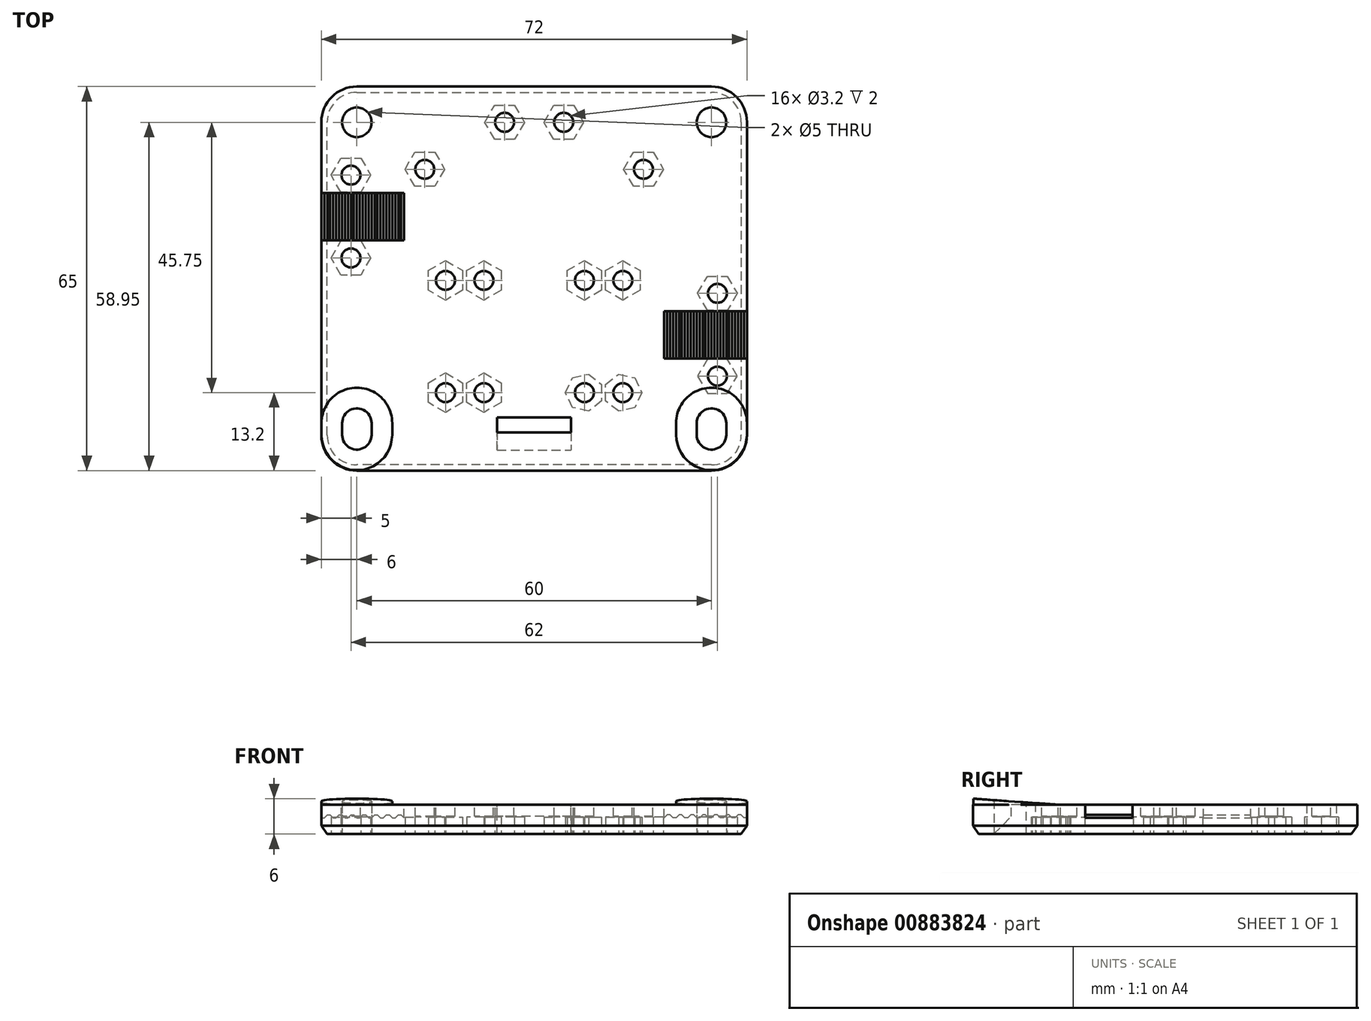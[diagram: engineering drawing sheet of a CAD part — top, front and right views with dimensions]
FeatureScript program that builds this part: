
annotation { "Feature Type Name" : "Feature", "Feature Type Description" : "" }
export const myFeature = defineFeature(function(context is Context, id is Id, definition is map)
    precondition{}
    {
        {
            var Q0;
            Q0=qCreatedBy(makeId("Top.planeOp"),FACE);
            var sketch = newSketch(context, id + "F0", { "sketchPlane" : qUnion([Q0])});
            skPoint(sketch, "E0.0", {"position": v(-36, 32.5) * mm});
            skPoint(sketch, "E0.3", {"position": v(36, 32.5) * mm});
            skPoint(sketch, "E1.1", {"position": v(-36, -32.5) * mm});
            skPoint(sketch, "E1.2", {"position": v(-36, -32.5) * mm});
            skPoint(sketch, "E1.3", {"position": v(36, -32.5) * mm});
            skLineSegment(sketch, "E2", {"start": v(36, -32.5) * mm, "end": v(-36, -32.5) * mm});
            skLineSegment(sketch, "E3", {"start": v(-36, 32.5) * mm, "end": v(36, 32.5) * mm});
            skLineSegment(sketch, "E4", {"start": v(36, 32.5) * mm, "end": v(36, -32.5) * mm});
            skLineSegment(sketch, "E5", {"start": v(-36, 32.5) * mm, "end": v(-36, -32.5) * mm});
            skLineSegment(sketch, "E6", {"start": v(-41.73, 0) * mm, "end": v(49.5, 0) * mm, "construction": true});
            skLineSegment(sketch, "E7", {"start": v(0, 42.12) * mm, "end": v(0, -49.86) * mm, "construction": true});
            skCircle(sketch, "E8", {"center": v(-30, 26.45) * mm, "radius": 2.5 * mm});
            skLineSegment(sketch, "E9", {"start": v(-37.66, 26.45) * mm, "end": v(41.82, 26.45) * mm, "construction": true});
            skLineSegment(sketch, "E10", {"start": v(-30, 35.76) * mm, "end": v(-30, -37.8) * mm, "construction": true});
            skLineSegment(sketch, "E11", {"start": v(30, 35.76) * mm, "end": v(30, -35.32) * mm, "construction": true});
            skPoint(sketch, "E12.0", {"position": v(-32.5, -26.45) * mm});
            skPoint(sketch, "E12.1", {"position": v(-27.5, -26.45) * mm});
            skPoint(sketch, "E13.0", {"position": v(-27.5, -24.45) * mm});
            skPoint(sketch, "E13.1", {"position": v(-32.5, -24.45) * mm});
            skLineSegment(sketch, "E14", {"start": v(-32.5, -24.45) * mm, "end": v(-32.5, -26.45) * mm});
            skLineSegment(sketch, "E15", {"start": v(-27.5, -24.45) * mm, "end": v(-27.5, -26.45) * mm});
            skLineSegment(sketch, "E16", {"start": v(-41.04, -25.45) * mm, "end": v(38.37, -25.45) * mm, "construction": true});
            skPoint(sketch, "E16.startSnap0", {"position": v(-32.5, -25.45) * mm});
            skArc(sketch, "E17", {"start": v(-27.5, -24.45) * mm, "mid": v(-30, -21.95) * mm, "end": v(-32.5, -24.45) * mm});
            skArc(sketch, "E18", {"start": v(-32.5, -26.45) * mm, "mid": v(-30, -28.95) * mm, "end": v(-27.5, -26.45) * mm});
            skLineSegment(sketch, "E19", {"start": v(27.5, -24.45) * mm, "end": v(27.5, -26.45) * mm});
            skLineSegment(sketch, "E20", {"start": v(32.5, -24.45) * mm, "end": v(32.5, -26.45) * mm});
            skArc(sketch, "E21", {"start": v(32.5, -24.45) * mm, "mid": v(30, -21.95) * mm, "end": v(27.5, -24.45) * mm});
            skArc(sketch, "E22", {"start": v(27.5, -26.45) * mm, "mid": v(30, -28.95) * mm, "end": v(32.5, -26.45) * mm});
            skCircle(sketch, "E23", {"center": v(30, 26.45) * mm, "radius": 2.5 * mm});
            skSolve(sketch);
        }
        {
            var Q0;
            Q0=makeQuery(id+"F0.imprint","IMPRINT",FACE,{"disambiguationData":[TD([[makeQuery(id+"F0.imprint","IMPRINT",EDGE,{"derivedFrom":sQuery(id+"F0.wireOp",EDGE,"E2")}),-1.0]])]});
            extrude(context, id + "F1", {"entities" : qUnion([Q0]), "depth" : 5 * mm, "offsetDistance" : 25 * mm});
        }
        {
            var Q0;
            Q0=makeQuery(id+"F1.opExtrude","SWEPT_EDGE",EDGE,{"disambiguationData":[OSD([sQuery(id+"F0.wireOp",EDGE,"E3"),sQuery(id+"F0.wireOp",EDGE,"E5")])]});
            var Q1;
            Q1=makeQuery(id+"F1.opExtrude","SWEPT_EDGE",EDGE,{"disambiguationData":[OSD([sQuery(id+"F0.wireOp",EDGE,"E3"),sQuery(id+"F0.wireOp",EDGE,"E4")])]});
            var Q2;
            Q2=makeQuery(id+"F1.opExtrude","SWEPT_EDGE",EDGE,{"disambiguationData":[OSD([sQuery(id+"F0.wireOp",EDGE,"E2"),sQuery(id+"F0.wireOp",EDGE,"E4")])]});
            var Q3;
            Q3=makeQuery(id+"F1.opExtrude","SWEPT_EDGE",EDGE,{"disambiguationData":[OSD([sQuery(id+"F0.wireOp",EDGE,"E2"),sQuery(id+"F0.wireOp",EDGE,"E5")])]});
            fillet(context, id + "F2", {"entities" : qUnion([Q0, Q1, Q2, Q3]), "radius" : 6 * mm, "tangentPropagation" : true, "allowEdgeOverflow" : false});
        }
        {
            var Q0;
            Q0=makeQuery(id+"F1.opExtrude","CAP_FACE",FACE,{"disambiguationData":[OSD([sQuery(id+"F0.wireOp",EDGE,"E2"),sQuery(id+"F0.wireOp",EDGE,"E3"),sQuery(id+"F0.wireOp",EDGE,"E4"),sQuery(id+"F0.wireOp",EDGE,"E5"),sQuery(id+"F0.wireOp",EDGE,"E8"),sQuery(id+"F0.wireOp",EDGE,"E14"),sQuery(id+"F0.wireOp",EDGE,"E15"),sQuery(id+"F0.wireOp",EDGE,"E17"),sQuery(id+"F0.wireOp",EDGE,"E18"),sQuery(id+"F0.wireOp",EDGE,"E19"),sQuery(id+"F0.wireOp",EDGE,"E20"),sQuery(id+"F0.wireOp",EDGE,"E21"),sQuery(id+"F0.wireOp",EDGE,"E22"),sQuery(id+"F0.wireOp",EDGE,"E23")])],"isStart":false});
            var sketch = newSketch(context, id + "F3", { "sketchPlane" : qUnion([Q0])});
            skCircle(sketch, "E24", {"center": v(31, -2.5) * mm, "radius": 1.6 * mm});
            skCircle(sketch, "E25", {"center": v(31, -16.5) * mm, "radius": 1.6 * mm});
            skLineSegment(sketch, "E26", {"start": v(36, -5.5) * mm, "end": v(22, -5.5) * mm});
            skLineSegment(sketch, "E27", {"start": v(22, -5.5) * mm, "end": v(22, -13.5) * mm});
            skLineSegment(sketch, "E28", {"start": v(22, -13.5) * mm, "end": v(36, -13.5) * mm});
            skLineSegment(sketch, "E29", {"start": v(36, -13.5) * mm, "end": v(36, -5.5) * mm});
            skLineSegment(sketch, "E30.0", {"start": v(36, 32.5) * mm, "end": v(36, -32.5) * mm});
            skLineSegment(sketch, "E31.bottom", {"start": v(-36, 14.5) * mm, "end": v(-22, 14.5) * mm});
            skLineSegment(sketch, "E31.top", {"start": v(-36, 6.5) * mm, "end": v(-22, 6.5) * mm});
            skLineSegment(sketch, "E31.left", {"start": v(-36, 14.5) * mm, "end": v(-36, 6.5) * mm});
            skLineSegment(sketch, "E31.right", {"start": v(-22, 14.5) * mm, "end": v(-22, 6.5) * mm});
            skLineSegment(sketch, "E32.0", {"start": v(-36, 32.5) * mm, "end": v(-36, -32.5) * mm});
            skCircle(sketch, "E33", {"center": v(-31, 17.5) * mm, "radius": 1.6 * mm});
            skCircle(sketch, "E34", {"center": v(-31, 3.5) * mm, "radius": 1.6 * mm});
            skCircle(sketch, "E35", {"center": v(-5, 26.45) * mm, "radius": 1.6 * mm});
            skCircle(sketch, "E36", {"center": v(5, 26.45) * mm, "radius": 1.6 * mm});
            skCircle(sketch, "E37", {"center": v(-8.5, -0.3) * mm, "radius": 1.6 * mm});
            skCircle(sketch, "E38", {"center": v(8.5, -0.3) * mm, "radius": 1.6 * mm});
            skCircle(sketch, "E39", {"center": v(-8.5, -19.3) * mm, "radius": 1.6 * mm});
            skCircle(sketch, "E40", {"center": v(8.5, -19.3) * mm, "radius": 1.6 * mm});
            skCircle(sketch, "E41", {"center": v(15, -0.3) * mm, "radius": 1.6 * mm});
            skCircle(sketch, "E42", {"center": v(15, -19.3) * mm, "radius": 1.6 * mm});
            skCircle(sketch, "E43", {"center": v(-15, -19.3) * mm, "radius": 1.6 * mm});
            skCircle(sketch, "E44", {"center": v(-15, -0.3) * mm, "radius": 1.6 * mm});
            skArc(sketch, "E45.0", {"start": v(-24, -24.45) * mm, "mid": v(-30, -18.45) * mm, "end": v(-36, -24.45) * mm});
            skLineSegment(sketch, "E45.1", {"start": v(-24, -24.45) * mm, "end": v(-24, -26.45) * mm});
            skArc(sketch, "E45.2", {"start": v(-36, -26.45) * mm, "mid": v(-30, -32.45) * mm, "end": v(-24, -26.45) * mm});
            skLineSegment(sketch, "E45.3", {"start": v(-36, -24.45) * mm, "end": v(-36, -26.45) * mm});
            skArc(sketch, "E46.0", {"start": v(36, -24.45) * mm, "mid": v(30, -18.45) * mm, "end": v(24, -24.45) * mm});
            skLineSegment(sketch, "E46.1", {"start": v(36, -24.45) * mm, "end": v(36, -26.45) * mm});
            skArc(sketch, "E46.2", {"start": v(24, -26.45) * mm, "mid": v(30, -32.45) * mm, "end": v(36, -26.45) * mm});
            skLineSegment(sketch, "E46.3", {"start": v(24, -24.45) * mm, "end": v(24, -26.45) * mm});
            skCircle(sketch, "E47", {"center": v(13, -26.5) * mm, "radius": 1.6 * mm});
            skCircle(sketch, "E48", {"center": v(-13, -26.5) * mm, "radius": 1.6 * mm});
            skLineSegment(sketch, "E49.bottom", {"start": v(-6.25, -23.5) * mm, "end": v(6.25, -23.5) * mm});
            skLineSegment(sketch, "E49.top", {"start": v(-6.25, -26) * mm, "end": v(6.25, -26) * mm});
            skLineSegment(sketch, "E49.left", {"start": v(-6.25, -23.5) * mm, "end": v(-6.25, -26) * mm});
            skLineSegment(sketch, "E49.right", {"start": v(6.25, -23.5) * mm, "end": v(6.25, -26) * mm});
            skCircle(sketch, "E50", {"center": v(-18.5, 18.5) * mm, "radius": 1.6 * mm});
            skCircle(sketch, "E51", {"center": v(18.5, 18.5) * mm, "radius": 1.6 * mm});
            skSolve(sketch);
        }
        {
            var Q0;
            {var subQ0=sQuery(id+"F3.wireOp",EDGE,"E31.bottom");Q0=makeQuery(id+"F3.imprint","IMPRINT",FACE,{"disambiguationData":[TD([[makeQuery(id+"F3.imprint","IMPRINT",EDGE,{"derivedFrom":subQ0}),-1.0]])]});}
            var Q1;
            {var subQ0=sQuery(id+"F3.wireOp",EDGE,"E26");Q1=makeQuery(id+"F3.imprint","IMPRINT",FACE,{"disambiguationData":[TD([[makeQuery(id+"F3.imprint","IMPRINT",EDGE,{"derivedFrom":subQ0}),1.0]])]});}
            extrude(context, id + "F4", {"entities" : qUnion([Q0, Q1]), "operationType" : NewBodyOperationType.REMOVE, "oppositeDirection" : true, "depth" : 2.25 * mm, "offsetDistance" : 25 * mm});
        }
        {
            var Q0;
            Q0=makeQuery(id+"F3.imprint","IMPRINT",FACE,{"disambiguationData":[TD([[makeQuery(id+"F3.imprint","IMPRINT",EDGE,{"derivedFrom":sQuery(id+"F3.wireOp",EDGE,"E36")}),1.0]])]});
            var Q1;
            Q1=makeQuery(id+"F3.imprint","IMPRINT",FACE,{"disambiguationData":[TD([[makeQuery(id+"F3.imprint","IMPRINT",EDGE,{"derivedFrom":sQuery(id+"F3.wireOp",EDGE,"E35")}),1.0]])]});
            var Q2;
            Q2=makeQuery(id+"F3.imprint","IMPRINT",FACE,{"disambiguationData":[TD([[makeQuery(id+"F3.imprint","IMPRINT",EDGE,{"derivedFrom":sQuery(id+"F3.wireOp",EDGE,"E33")}),1.0]])]});
            var Q3;
            Q3=makeQuery(id+"F3.imprint","IMPRINT",FACE,{"disambiguationData":[TD([[makeQuery(id+"F3.imprint","IMPRINT",EDGE,{"derivedFrom":sQuery(id+"F3.wireOp",EDGE,"E34")}),1.0]])]});
            var Q4;
            Q4=makeQuery(id+"F3.imprint","IMPRINT",FACE,{"disambiguationData":[TD([[makeQuery(id+"F3.imprint","IMPRINT",EDGE,{"derivedFrom":sQuery(id+"F3.wireOp",EDGE,"E24")}),1.0]])]});
            var Q5;
            Q5=makeQuery(id+"F3.imprint","IMPRINT",FACE,{"disambiguationData":[TD([[makeQuery(id+"F3.imprint","IMPRINT",EDGE,{"derivedFrom":sQuery(id+"F3.wireOp",EDGE,"E25")}),1.0]])]});
            var Q6;
            Q6=makeQuery(id+"F3.imprint","IMPRINT",FACE,{"disambiguationData":[TD([[makeQuery(id+"F3.imprint","IMPRINT",EDGE,{"derivedFrom":sQuery(id+"F3.wireOp",EDGE,"E44")}),1.0]])]});
            var Q7;
            Q7=makeQuery(id+"F3.imprint","IMPRINT",FACE,{"disambiguationData":[TD([[makeQuery(id+"F3.imprint","IMPRINT",EDGE,{"derivedFrom":sQuery(id+"F3.wireOp",EDGE,"E37")}),1.0]])]});
            var Q8;
            Q8=makeQuery(id+"F3.imprint","IMPRINT",FACE,{"disambiguationData":[TD([[makeQuery(id+"F3.imprint","IMPRINT",EDGE,{"derivedFrom":sQuery(id+"F3.wireOp",EDGE,"E38")}),1.0]])]});
            var Q9;
            Q9=makeQuery(id+"F3.imprint","IMPRINT",FACE,{"disambiguationData":[TD([[makeQuery(id+"F3.imprint","IMPRINT",EDGE,{"derivedFrom":sQuery(id+"F3.wireOp",EDGE,"E41")}),1.0]])]});
            var Q10;
            Q10=makeQuery(id+"F3.imprint","IMPRINT",FACE,{"disambiguationData":[TD([[makeQuery(id+"F3.imprint","IMPRINT",EDGE,{"derivedFrom":sQuery(id+"F3.wireOp",EDGE,"E42")}),1.0]])]});
            var Q11;
            Q11=makeQuery(id+"F3.imprint","IMPRINT",FACE,{"disambiguationData":[TD([[makeQuery(id+"F3.imprint","IMPRINT",EDGE,{"derivedFrom":sQuery(id+"F3.wireOp",EDGE,"E40")}),1.0]])]});
            var Q12;
            Q12=makeQuery(id+"F3.imprint","IMPRINT",FACE,{"disambiguationData":[TD([[makeQuery(id+"F3.imprint","IMPRINT",EDGE,{"derivedFrom":sQuery(id+"F3.wireOp",EDGE,"E39")}),1.0]])]});
            var Q13;
            Q13=makeQuery(id+"F3.imprint","IMPRINT",FACE,{"disambiguationData":[TD([[makeQuery(id+"F3.imprint","IMPRINT",EDGE,{"derivedFrom":sQuery(id+"F3.wireOp",EDGE,"E43")}),1.0]])]});
            var Q14;
            Q14=makeQuery(id+"F3.imprint","IMPRINT",FACE,{"disambiguationData":[TD([[makeQuery(id+"F3.imprint","IMPRINT",EDGE,{"derivedFrom":sQuery(id+"F3.wireOp",EDGE,"E50")}),1.0]])]});
            var Q15;
            Q15=makeQuery(id+"F3.imprint","IMPRINT",FACE,{"disambiguationData":[TD([[makeQuery(id+"F3.imprint","IMPRINT",EDGE,{"derivedFrom":sQuery(id+"F3.wireOp",EDGE,"E51")}),1.0]])]});
            extrude(context, id + "F5", {"entities" : qUnion([Q0, Q1, Q2, Q3, Q4, Q5, Q6, Q7, Q8, Q9, Q10, Q11, Q12, Q13, Q14, Q15]), "operationType" : NewBodyOperationType.REMOVE, "oppositeDirection" : true, "depth" : 2 * mm, "offsetDistance" : 25 * mm});
        }
        {
            var Q0;
            Q0=makeQuery(id+"F0.imprint","IMPRINT",FACE,{"disambiguationData":[TD([[makeQuery(id+"F0.imprint","IMPRINT",EDGE,{"derivedFrom":sQuery(id+"F0.wireOp",EDGE,"E2")}),-1.0]])]});
            var sketch = newSketch(context, id + "F6", { "sketchPlane" : qUnion([Q0])});
            skCircle(sketch, "E52.cCircle", {"center": v(31, -16.5) * mm, "radius": 2.9 * mm, "construction": true});
            skLineSegment(sketch, "E52.0", {"start": v(32.67, -13.6) * mm, "end": v(29.33, -13.6) * mm});
            skLineSegment(sketch, "E52.1", {"start": v(34.35, -16.5) * mm, "end": v(32.67, -13.6) * mm});
            skLineSegment(sketch, "E52.2", {"start": v(32.67, -19.4) * mm, "end": v(34.35, -16.5) * mm});
            skLineSegment(sketch, "E52.3", {"start": v(29.33, -19.4) * mm, "end": v(32.67, -19.4) * mm});
            skLineSegment(sketch, "E52.4", {"start": v(27.65, -16.5) * mm, "end": v(29.33, -19.4) * mm});
            skLineSegment(sketch, "E52.5", {"start": v(29.33, -13.6) * mm, "end": v(27.65, -16.5) * mm});
            skPoint(sketch, "E52.0.midPoint", {"position": v(31, -13.6) * mm});
            skCircle(sketch, "E53.cCircle", {"center": v(31, -2.5) * mm, "radius": 2.9 * mm, "construction": true});
            skLineSegment(sketch, "E53.0", {"start": v(32.67, -5.4) * mm, "end": v(29.33, -5.4) * mm});
            skLineSegment(sketch, "E53.1", {"start": v(29.33, -5.4) * mm, "end": v(27.65, -2.5) * mm});
            skLineSegment(sketch, "E53.2", {"start": v(27.65, -2.5) * mm, "end": v(29.33, 0.4) * mm});
            skLineSegment(sketch, "E53.3", {"start": v(29.33, 0.4) * mm, "end": v(32.67, 0.4) * mm});
            skLineSegment(sketch, "E53.4", {"start": v(32.67, 0.4) * mm, "end": v(34.35, -2.5) * mm});
            skLineSegment(sketch, "E53.5", {"start": v(34.35, -2.5) * mm, "end": v(32.67, -5.4) * mm});
            skPoint(sketch, "E53.0.midPoint", {"position": v(31, -5.4) * mm});
            skPoint(sketch, "E54.0", {"position": v(-31, 3.5) * mm});
            skPoint(sketch, "E54.1", {"position": v(-31, 17.5) * mm});
            skPoint(sketch, "E54.2", {"position": v(-5, 26.45) * mm});
            skPoint(sketch, "E54.3", {"position": v(5, 26.45) * mm});
            skCircle(sketch, "E55.cCircle", {"center": v(-31, 3.5) * mm, "radius": 2.9 * mm, "construction": true});
            skLineSegment(sketch, "E55.0", {"start": v(-32.67, 6.4) * mm, "end": v(-29.33, 6.4) * mm});
            skLineSegment(sketch, "E55.1", {"start": v(-29.33, 6.4) * mm, "end": v(-27.65, 3.5) * mm});
            skLineSegment(sketch, "E55.2", {"start": v(-27.65, 3.5) * mm, "end": v(-29.33, 0.6) * mm});
            skLineSegment(sketch, "E55.3", {"start": v(-29.33, 0.6) * mm, "end": v(-32.67, 0.6) * mm});
            skLineSegment(sketch, "E55.4", {"start": v(-32.67, 0.6) * mm, "end": v(-34.35, 3.5) * mm});
            skLineSegment(sketch, "E55.5", {"start": v(-34.35, 3.5) * mm, "end": v(-32.67, 6.4) * mm});
            skPoint(sketch, "E55.0.midPoint", {"position": v(-31, 6.4) * mm});
            skCircle(sketch, "E56.cCircle", {"center": v(-31, 17.5) * mm, "radius": 2.9 * mm, "construction": true});
            skLineSegment(sketch, "E56.0", {"start": v(-32.67, 20.4) * mm, "end": v(-29.33, 20.4) * mm});
            skLineSegment(sketch, "E56.1", {"start": v(-29.33, 20.4) * mm, "end": v(-27.65, 17.5) * mm});
            skLineSegment(sketch, "E56.2", {"start": v(-27.65, 17.5) * mm, "end": v(-29.33, 14.6) * mm});
            skLineSegment(sketch, "E56.3", {"start": v(-29.33, 14.6) * mm, "end": v(-32.67, 14.6) * mm});
            skLineSegment(sketch, "E56.4", {"start": v(-32.67, 14.6) * mm, "end": v(-34.35, 17.5) * mm});
            skLineSegment(sketch, "E56.5", {"start": v(-34.35, 17.5) * mm, "end": v(-32.67, 20.4) * mm});
            skPoint(sketch, "E56.0.midPoint", {"position": v(-31, 20.4) * mm});
            skCircle(sketch, "E57.cCircle", {"center": v(5, 26.45) * mm, "radius": 2.9 * mm, "construction": true});
            skLineSegment(sketch, "E57.0", {"start": v(6.67, 23.55) * mm, "end": v(3.33, 23.55) * mm});
            skLineSegment(sketch, "E57.1", {"start": v(3.33, 23.55) * mm, "end": v(1.65, 26.45) * mm});
            skLineSegment(sketch, "E57.2", {"start": v(1.65, 26.45) * mm, "end": v(3.33, 29.35) * mm});
            skLineSegment(sketch, "E57.3", {"start": v(3.33, 29.35) * mm, "end": v(6.67, 29.35) * mm});
            skLineSegment(sketch, "E57.4", {"start": v(6.67, 29.35) * mm, "end": v(8.35, 26.45) * mm});
            skLineSegment(sketch, "E57.5", {"start": v(8.35, 26.45) * mm, "end": v(6.67, 23.55) * mm});
            skPoint(sketch, "E57.0.midPoint", {"position": v(5, 23.55) * mm});
            skCircle(sketch, "E58.cCircle", {"center": v(-5, 26.45) * mm, "radius": 2.9 * mm, "construction": true});
            skLineSegment(sketch, "E58.0", {"start": v(-3.33, 23.55) * mm, "end": v(-6.67, 23.55) * mm});
            skLineSegment(sketch, "E58.1", {"start": v(-6.67, 23.55) * mm, "end": v(-8.35, 26.45) * mm});
            skLineSegment(sketch, "E58.2", {"start": v(-8.35, 26.45) * mm, "end": v(-6.67, 29.35) * mm});
            skLineSegment(sketch, "E58.3", {"start": v(-6.67, 29.35) * mm, "end": v(-3.33, 29.35) * mm});
            skLineSegment(sketch, "E58.4", {"start": v(-3.33, 29.35) * mm, "end": v(-1.65, 26.45) * mm});
            skLineSegment(sketch, "E58.5", {"start": v(-1.65, 26.45) * mm, "end": v(-3.33, 23.55) * mm});
            skPoint(sketch, "E58.0.midPoint", {"position": v(-5, 23.55) * mm});
            skPoint(sketch, "E59.0", {"position": v(15, -0.3) * mm});
            skPoint(sketch, "E59.1", {"position": v(8.5, -0.3) * mm});
            skPoint(sketch, "E59.2", {"position": v(-8.5, -0.3) * mm});
            skPoint(sketch, "E59.3", {"position": v(-15, -0.3) * mm});
            skPoint(sketch, "E59.4", {"position": v(-15, -19.3) * mm});
            skPoint(sketch, "E59.5", {"position": v(-8.5, -19.3) * mm});
            skPoint(sketch, "E59.6", {"position": v(8.5, -19.3) * mm});
            skPoint(sketch, "E59.7", {"position": v(15, -19.3) * mm});
            skCircle(sketch, "E60.cCircle", {"center": v(15, -0.3) * mm, "radius": 2.9 * mm, "construction": true});
            skLineSegment(sketch, "E60.0", {"start": v(12.1, -1.97) * mm, "end": v(12.1, 1.37) * mm});
            skLineSegment(sketch, "E60.1", {"start": v(12.1, 1.37) * mm, "end": v(15, 3.05) * mm});
            skLineSegment(sketch, "E60.2", {"start": v(15, 3.05) * mm, "end": v(17.9, 1.37) * mm});
            skLineSegment(sketch, "E60.3", {"start": v(17.9, 1.37) * mm, "end": v(17.9, -1.97) * mm});
            skLineSegment(sketch, "E60.4", {"start": v(17.9, -1.97) * mm, "end": v(15, -3.65) * mm});
            skLineSegment(sketch, "E60.5", {"start": v(15, -3.65) * mm, "end": v(12.1, -1.97) * mm});
            skPoint(sketch, "E60.0.midPoint", {"position": v(12.1, -0.3) * mm});
            skCircle(sketch, "E61.cCircle", {"center": v(8.5, -0.3) * mm, "radius": 2.9 * mm, "construction": true});
            skLineSegment(sketch, "E61.0", {"start": v(11.4, 1.37) * mm, "end": v(11.4, -1.97) * mm});
            skLineSegment(sketch, "E61.1", {"start": v(11.4, -1.97) * mm, "end": v(8.5, -3.65) * mm});
            skLineSegment(sketch, "E61.2", {"start": v(8.5, -3.65) * mm, "end": v(5.6, -1.97) * mm});
            skLineSegment(sketch, "E61.3", {"start": v(5.6, -1.97) * mm, "end": v(5.6, 1.37) * mm});
            skLineSegment(sketch, "E61.4", {"start": v(5.6, 1.37) * mm, "end": v(8.5, 3.05) * mm});
            skLineSegment(sketch, "E61.5", {"start": v(8.5, 3.05) * mm, "end": v(11.4, 1.37) * mm});
            skPoint(sketch, "E61.0.midPoint", {"position": v(11.4, -0.3) * mm});
            skCircle(sketch, "E62.cCircle", {"center": v(-8.5, -0.3) * mm, "radius": 2.9 * mm, "construction": true});
            skLineSegment(sketch, "E62.0", {"start": v(-11.4, -1.97) * mm, "end": v(-11.4, 1.37) * mm});
            skLineSegment(sketch, "E62.1", {"start": v(-11.4, 1.37) * mm, "end": v(-8.5, 3.05) * mm});
            skLineSegment(sketch, "E62.2", {"start": v(-8.5, 3.05) * mm, "end": v(-5.6, 1.37) * mm});
            skLineSegment(sketch, "E62.3", {"start": v(-5.6, 1.37) * mm, "end": v(-5.6, -1.97) * mm});
            skLineSegment(sketch, "E62.4", {"start": v(-5.6, -1.97) * mm, "end": v(-8.5, -3.65) * mm});
            skLineSegment(sketch, "E62.5", {"start": v(-8.5, -3.65) * mm, "end": v(-11.4, -1.97) * mm});
            skPoint(sketch, "E62.0.midPoint", {"position": v(-11.4, -0.3) * mm});
            skCircle(sketch, "E63.cCircle", {"center": v(-15, -0.3) * mm, "radius": 2.9 * mm, "construction": true});
            skLineSegment(sketch, "E63.0", {"start": v(-12.1, 1.37) * mm, "end": v(-12.1, -1.97) * mm});
            skLineSegment(sketch, "E63.1", {"start": v(-12.1, -1.97) * mm, "end": v(-15, -3.65) * mm});
            skLineSegment(sketch, "E63.2", {"start": v(-15, -3.65) * mm, "end": v(-17.9, -1.97) * mm});
            skLineSegment(sketch, "E63.3", {"start": v(-17.9, -1.97) * mm, "end": v(-17.9, 1.37) * mm});
            skLineSegment(sketch, "E63.4", {"start": v(-17.9, 1.37) * mm, "end": v(-15, 3.05) * mm});
            skLineSegment(sketch, "E63.5", {"start": v(-15, 3.05) * mm, "end": v(-12.1, 1.37) * mm});
            skPoint(sketch, "E63.0.midPoint", {"position": v(-12.1, -0.3) * mm});
            skCircle(sketch, "E64.cCircle", {"center": v(-15, -19.3) * mm, "radius": 2.9 * mm, "construction": true});
            skLineSegment(sketch, "E64.0", {"start": v(-12.1, -17.63) * mm, "end": v(-12.1, -20.97) * mm});
            skLineSegment(sketch, "E64.1", {"start": v(-12.1, -20.97) * mm, "end": v(-15, -22.65) * mm});
            skLineSegment(sketch, "E64.2", {"start": v(-15, -22.65) * mm, "end": v(-17.9, -20.97) * mm});
            skLineSegment(sketch, "E64.3", {"start": v(-17.9, -20.97) * mm, "end": v(-17.9, -17.63) * mm});
            skLineSegment(sketch, "E64.4", {"start": v(-17.9, -17.63) * mm, "end": v(-15, -15.95) * mm});
            skLineSegment(sketch, "E64.5", {"start": v(-15, -15.95) * mm, "end": v(-12.1, -17.63) * mm});
            skPoint(sketch, "E64.0.midPoint", {"position": v(-12.1, -19.3) * mm});
            skCircle(sketch, "E65.cCircle", {"center": v(-8.5, -19.3) * mm, "radius": 2.9 * mm, "construction": true});
            skLineSegment(sketch, "E65.0", {"start": v(-11.4, -20.97) * mm, "end": v(-11.4, -17.63) * mm});
            skLineSegment(sketch, "E65.1", {"start": v(-11.4, -17.63) * mm, "end": v(-8.5, -15.95) * mm});
            skLineSegment(sketch, "E65.2", {"start": v(-8.5, -15.95) * mm, "end": v(-5.6, -17.63) * mm});
            skLineSegment(sketch, "E65.3", {"start": v(-5.6, -17.63) * mm, "end": v(-5.6, -20.97) * mm});
            skLineSegment(sketch, "E65.4", {"start": v(-5.6, -20.97) * mm, "end": v(-8.5, -22.65) * mm});
            skLineSegment(sketch, "E65.5", {"start": v(-8.5, -22.65) * mm, "end": v(-11.4, -20.97) * mm});
            skPoint(sketch, "E65.0.midPoint", {"position": v(-11.4, -19.3) * mm});
            skCircle(sketch, "E66.cCircle", {"center": v(8.5, -19.3) * mm, "radius": 2.9 * mm, "construction": true});
            skLineSegment(sketch, "E66.0", {"start": v(11.4, -17.9) * mm, "end": v(11.4, -20.7) * mm});
            skLineSegment(sketch, "E66.1", {"start": v(11.4, -20.7) * mm, "end": v(9.22, -22.44) * mm});
            skLineSegment(sketch, "E66.2", {"start": v(9.22, -22.44) * mm, "end": v(6.5, -21.82) * mm});
            skLineSegment(sketch, "E66.3", {"start": v(6.5, -21.82) * mm, "end": v(5.28, -19.3) * mm});
            skLineSegment(sketch, "E66.4", {"start": v(5.28, -19.3) * mm, "end": v(6.5, -16.78) * mm});
            skLineSegment(sketch, "E66.5", {"start": v(6.5, -16.78) * mm, "end": v(9.22, -16.16) * mm});
            skLineSegment(sketch, "E66.6", {"start": v(9.22, -16.16) * mm, "end": v(11.4, -17.9) * mm});
            skPoint(sketch, "E66.0.midPoint", {"position": v(11.4, -19.3) * mm});
            skCircle(sketch, "E67.cCircle", {"center": v(15, -19.3) * mm, "radius": 2.9 * mm, "construction": true});
            skLineSegment(sketch, "E67.0", {"start": v(17, -16.78) * mm, "end": v(18.22, -19.3) * mm});
            skLineSegment(sketch, "E67.1", {"start": v(18.22, -19.3) * mm, "end": v(17, -21.82) * mm});
            skLineSegment(sketch, "E67.2", {"start": v(17, -21.82) * mm, "end": v(14.28, -22.44) * mm});
            skLineSegment(sketch, "E67.3", {"start": v(14.28, -22.44) * mm, "end": v(12.1, -20.7) * mm});
            skLineSegment(sketch, "E67.4", {"start": v(12.1, -20.7) * mm, "end": v(12.1, -17.9) * mm});
            skLineSegment(sketch, "E67.5", {"start": v(12.1, -17.9) * mm, "end": v(14.28, -16.16) * mm});
            skLineSegment(sketch, "E67.6", {"start": v(14.28, -16.16) * mm, "end": v(17, -16.78) * mm});
            skPoint(sketch, "E68.0", {"position": v(18.5, 18.5) * mm});
            skPoint(sketch, "E68.1", {"position": v(-18.5, 18.5) * mm});
            skCircle(sketch, "E69.cCircle", {"center": v(18.5, 18.5) * mm, "radius": 2.9 * mm, "construction": true});
            skLineSegment(sketch, "E69.0", {"start": v(20.17, 15.6) * mm, "end": v(16.83, 15.6) * mm});
            skLineSegment(sketch, "E69.1", {"start": v(16.83, 15.6) * mm, "end": v(15.15, 18.5) * mm});
            skLineSegment(sketch, "E69.2", {"start": v(15.15, 18.5) * mm, "end": v(16.83, 21.4) * mm});
            skLineSegment(sketch, "E69.3", {"start": v(16.83, 21.4) * mm, "end": v(20.17, 21.4) * mm});
            skLineSegment(sketch, "E69.4", {"start": v(20.17, 21.4) * mm, "end": v(21.85, 18.5) * mm});
            skLineSegment(sketch, "E69.5", {"start": v(21.85, 18.5) * mm, "end": v(20.17, 15.6) * mm});
            skPoint(sketch, "E69.0.midPoint", {"position": v(18.5, 15.6) * mm});
            skCircle(sketch, "E70.cCircle", {"center": v(-18.5, 18.5) * mm, "radius": 2.9 * mm, "construction": true});
            skLineSegment(sketch, "E70.0", {"start": v(-16.83, 15.6) * mm, "end": v(-20.17, 15.6) * mm});
            skLineSegment(sketch, "E70.1", {"start": v(-20.17, 15.6) * mm, "end": v(-21.85, 18.5) * mm});
            skLineSegment(sketch, "E70.2", {"start": v(-21.85, 18.5) * mm, "end": v(-20.17, 21.4) * mm});
            skLineSegment(sketch, "E70.3", {"start": v(-20.17, 21.4) * mm, "end": v(-16.83, 21.4) * mm});
            skLineSegment(sketch, "E70.4", {"start": v(-16.83, 21.4) * mm, "end": v(-15.15, 18.5) * mm});
            skLineSegment(sketch, "E70.5", {"start": v(-15.15, 18.5) * mm, "end": v(-16.83, 15.6) * mm});
            skPoint(sketch, "E70.0.midPoint", {"position": v(-18.5, 15.6) * mm});
            skSolve(sketch);
        }
        {
            var Q0;
            Q0=makeQuery(id+"F6.imprint","IMPRINT",FACE,{"disambiguationData":[TD([[makeQuery(id+"F6.imprint","IMPRINT",EDGE,{"derivedFrom":sQuery(id+"F6.wireOp",EDGE,"E56.0")}),-1.0]])]});
            var Q1;
            Q1=makeQuery(id+"F6.imprint","IMPRINT",FACE,{"disambiguationData":[TD([[makeQuery(id+"F6.imprint","IMPRINT",EDGE,{"derivedFrom":sQuery(id+"F6.wireOp",EDGE,"E55.0")}),-1.0]])]});
            var Q2;
            Q2=makeQuery(id+"F6.imprint","IMPRINT",FACE,{"disambiguationData":[TD([[makeQuery(id+"F6.imprint","IMPRINT",EDGE,{"derivedFrom":sQuery(id+"F6.wireOp",EDGE,"E58.0")}),-1.0]])]});
            var Q3;
            Q3=makeQuery(id+"F6.imprint","IMPRINT",FACE,{"disambiguationData":[TD([[makeQuery(id+"F6.imprint","IMPRINT",EDGE,{"derivedFrom":sQuery(id+"F6.wireOp",EDGE,"E57.0")}),-1.0]])]});
            var Q4;
            Q4=makeQuery(id+"F6.imprint","IMPRINT",FACE,{"disambiguationData":[TD([[makeQuery(id+"F6.imprint","IMPRINT",EDGE,{"derivedFrom":sQuery(id+"F6.wireOp",EDGE,"E53.0")}),-1.0]])]});
            var Q5;
            Q5=makeQuery(id+"F6.imprint","IMPRINT",FACE,{"disambiguationData":[TD([[makeQuery(id+"F6.imprint","IMPRINT",EDGE,{"derivedFrom":sQuery(id+"F6.wireOp",EDGE,"E52.0")}),1.0]])]});
            var Q6;
            Q6=makeQuery(id+"F6.imprint","IMPRINT",FACE,{"disambiguationData":[TD([[makeQuery(id+"F6.imprint","IMPRINT",EDGE,{"derivedFrom":sQuery(id+"F6.wireOp",EDGE,"E64.0")}),-1.0]])]});
            var Q7;
            Q7=makeQuery(id+"F6.imprint","IMPRINT",FACE,{"disambiguationData":[TD([[makeQuery(id+"F6.imprint","IMPRINT",EDGE,{"derivedFrom":sQuery(id+"F6.wireOp",EDGE,"E65.0")}),-1.0]])]});
            var Q8;
            Q8=makeQuery(id+"F6.imprint","IMPRINT",FACE,{"disambiguationData":[TD([[makeQuery(id+"F6.imprint","IMPRINT",EDGE,{"derivedFrom":sQuery(id+"F6.wireOp",EDGE,"E66.0")}),-1.0]])]});
            var Q9;
            Q9=makeQuery(id+"F6.imprint","IMPRINT",FACE,{"disambiguationData":[TD([[makeQuery(id+"F6.imprint","IMPRINT",EDGE,{"derivedFrom":sQuery(id+"F6.wireOp",EDGE,"E67.0")}),-1.0]])]});
            var Q10;
            Q10=makeQuery(id+"F6.imprint","IMPRINT",FACE,{"disambiguationData":[TD([[makeQuery(id+"F6.imprint","IMPRINT",EDGE,{"derivedFrom":sQuery(id+"F6.wireOp",EDGE,"E60.0")}),-1.0]])]});
            var Q11;
            Q11=makeQuery(id+"F6.imprint","IMPRINT",FACE,{"disambiguationData":[TD([[makeQuery(id+"F6.imprint","IMPRINT",EDGE,{"derivedFrom":sQuery(id+"F6.wireOp",EDGE,"E61.0")}),-1.0]])]});
            var Q12;
            Q12=makeQuery(id+"F6.imprint","IMPRINT",FACE,{"disambiguationData":[TD([[makeQuery(id+"F6.imprint","IMPRINT",EDGE,{"derivedFrom":sQuery(id+"F6.wireOp",EDGE,"E62.0")}),-1.0]])]});
            var Q13;
            Q13=makeQuery(id+"F6.imprint","IMPRINT",FACE,{"disambiguationData":[TD([[makeQuery(id+"F6.imprint","IMPRINT",EDGE,{"derivedFrom":sQuery(id+"F6.wireOp",EDGE,"E63.0")}),-1.0]])]});
            var Q14;
            Q14=makeQuery(id+"F6.imprint","IMPRINT",FACE,{"disambiguationData":[TD([[makeQuery(id+"F6.imprint","IMPRINT",EDGE,{"derivedFrom":sQuery(id+"F6.wireOp",EDGE,"E69.0")}),-1.0]])]});
            var Q15;
            Q15=makeQuery(id+"F6.imprint","IMPRINT",FACE,{"disambiguationData":[TD([[makeQuery(id+"F6.imprint","IMPRINT",EDGE,{"derivedFrom":sQuery(id+"F6.wireOp",EDGE,"E70.0")}),-1.0]])]});
            extrude(context, id + "F7", {"entities" : qUnion([Q0, Q1, Q2, Q3, Q4, Q5, Q6, Q7, Q8, Q9, Q10, Q11, Q12, Q13, Q14, Q15]), "operationType" : NewBodyOperationType.REMOVE, "depth" : 2.9 * mm, "offsetDistance" : 25 * mm});
        }
        {
            var Q0;
            Q0=makeQuery(id+"F3.imprint","IMPRINT",FACE,{"disambiguationData":[TD([[makeQuery(id+"F3.imprint","IMPRINT",EDGE,{"derivedFrom":sQuery(id+"F3.wireOp",EDGE,"E46.0")}),1.0]])]});
            var Q1;
            Q1=makeQuery(id+"F3.imprint","IMPRINT",FACE,{"disambiguationData":[TD([[makeQuery(id+"F3.imprint","IMPRINT",EDGE,{"derivedFrom":sQuery(id+"F3.wireOp",EDGE,"E45.0")}),1.0]])]});
            extrude(context, id + "F8", {"entities" : qUnion([Q0, Q1]), "operationType" : NewBodyOperationType.ADD, "depth" : 1 * mm, "offsetDistance" : 25 * mm});
        }
        {
            var Q0;
            Q0=makeQuery(id+"F8.boolean.opBoolean","MERGE",FACE,{"derivedFrom":[makeQuery(id+"F1.opExtrude","SWEPT_FACE",FACE,{"disambiguationData":[OSD([sQuery(id+"F0.wireOp",EDGE,"E4")])]}),makeQuery(id+"F8.opExtrude","SWEPT_FACE",FACE,{"disambiguationData":[OSD([sQuery(id+"F3.wireOp",EDGE,"E46.1")])]})]});
            var sketch = newSketch(context, id + "F9", { "sketchPlane" : qUnion([Q0])});
            skLineSegment(sketch, "E71", {"start": v(-18.45, 5) * mm, "end": v(-18.45, 6) * mm});
            skLineSegment(sketch, "E72", {"start": v(-18.45, 6) * mm, "end": v(-32.45, 6) * mm});
            skLineSegment(sketch, "E73", {"start": v(-32.45, 6) * mm, "end": v(-18.45, 5) * mm});
            skPoint(sketch, "E74.0", {"position": v(-18.45, 6) * mm});
            skPoint(sketch, "E75.0", {"position": v(-32.45, 6) * mm});
            skSolve(sketch);
        }
        {
            var Q0;
            {var subQ0=sQuery(id+"F9.wireOp",EDGE,"E72");var subQ1=sQuery(id+"F3.wireOp",EDGE,"E46.1");var subQ2=sQuery(id+"F3.wireOp",EDGE,"E30.0");var subQ3=makeQuery(id+"F8.opExtrude","SWEPT_EDGE",EDGE,{"disambiguationData":[OSD([subQ2,sQuery(id+"F3.wireOp",EDGE,"E46.0"),subQ1])]});var subQ4=makeQuery(id+"F9.imprint","INTERSECT",VERTEX,{"derivedFrom":[subQ3,subQ0]});Q0=makeQuery(id+"F9.imprint","IMPRINT",FACE,{"disambiguationData":[TD([[makeQuery(id+"F9.imprint","IMPRINT",EDGE,{"disambiguationData":[TD([[subQ4,-1.0]])],"derivedFrom":subQ0}),1.0]])]});}
            var Q1;
            {var subQ0=sQuery(id+"F9.wireOp",EDGE,"E71");Q1=makeQuery(id+"F9.imprint","IMPRINT",FACE,{"disambiguationData":[TD([[makeQuery(id+"F9.imprint","IMPRINT",EDGE,{"derivedFrom":subQ0}),1.0]])]});}
            var Q2;
            {var subQ0=sQuery(id+"F9.wireOp",EDGE,"E72");var subQ3=sQuery(id+"F9.wireOp",EDGE,"E73");var subQ4=makeQuery(id+"F9.imprint","INTERSECT",VERTEX,{"derivedFrom":[subQ0,subQ3]});Q2=makeQuery(id+"F9.imprint","IMPRINT",FACE,{"disambiguationData":[TD([[makeQuery(id+"F9.imprint","IMPRINT",EDGE,{"disambiguationData":[TD([[subQ4,1.0]])],"derivedFrom":subQ0}),1.0]])]});}
            extrude(context, id + "F10", {"entities" : qUnion([Q0, Q1, Q2]), "operationType" : NewBodyOperationType.REMOVE, "endBound" : BoundingType.THROUGH_ALL, "oppositeDirection" : true, "depth" : 25 * mm, "offsetDistance" : 25 * mm});
        }
        {
            var Q0;
            Q0=makeQuery(id+"F4.boolean.opBoolean","COPY",FACE,{"derivedFrom":makeQuery(id+"F4.opExtrude","SWEPT_FACE",FACE,{"disambiguationData":[OSD([sQuery(id+"F3.wireOp",EDGE,"E31.bottom")])]})});
            var sketch = newSketch(context, id + "F11", { "sketchPlane" : qUnion([Q0])});
            skLineSegment(sketch, "E76", {"start": v(-36, 2.75) * mm, "end": v(-35.5, 2.75) * mm});
            skLineSegment(sketch, "E77", {"start": v(-35.5, 2.75) * mm, "end": v(-35, 3.25) * mm});
            skLineSegment(sketch, "E78", {"start": v(-35, 3.25) * mm, "end": v(-34.5, 3.25) * mm});
            skLineSegment(sketch, "E79", {"start": v(-34.5, 3.25) * mm, "end": v(-34, 2.75) * mm});
            skLineSegment(sketch, "E80", {"start": v(-34, 2.75) * mm, "end": v(-33.5, 2.75) * mm});
            skLineSegment(sketch, "E81", {"start": v(-33.5, 2.75) * mm, "end": v(-33, 3.25) * mm});
            skLineSegment(sketch, "E82", {"start": v(-33, 3.25) * mm, "end": v(-32.5, 3.25) * mm});
            skLineSegment(sketch, "E83", {"start": v(-32.5, 3.25) * mm, "end": v(-32, 2.75) * mm});
            skLineSegment(sketch, "E84", {"start": v(-32, 2.75) * mm, "end": v(-31.5, 2.75) * mm});
            skLineSegment(sketch, "E85", {"start": v(-31.5, 2.75) * mm, "end": v(-31, 3.25) * mm});
            skLineSegment(sketch, "E86", {"start": v(-31, 3.25) * mm, "end": v(-30.5, 3.25) * mm});
            skLineSegment(sketch, "E87", {"start": v(-30.5, 3.25) * mm, "end": v(-30, 2.75) * mm});
            skLineSegment(sketch, "E88", {"start": v(-30, 2.75) * mm, "end": v(-29.5, 2.75) * mm});
            skLineSegment(sketch, "E89", {"start": v(-29.5, 2.75) * mm, "end": v(-29, 3.25) * mm});
            skLineSegment(sketch, "E90", {"start": v(-29, 3.25) * mm, "end": v(-28.5, 3.25) * mm});
            skLineSegment(sketch, "E91", {"start": v(-28.5, 3.25) * mm, "end": v(-28, 2.75) * mm});
            skLineSegment(sketch, "E92", {"start": v(-28, 2.75) * mm, "end": v(-27.5, 2.75) * mm});
            skLineSegment(sketch, "E93", {"start": v(-27.5, 2.75) * mm, "end": v(-27, 3.25) * mm});
            skLineSegment(sketch, "E94", {"start": v(-27, 3.25) * mm, "end": v(-26.5, 3.25) * mm});
            skLineSegment(sketch, "E95", {"start": v(-26.5, 3.25) * mm, "end": v(-26, 2.75) * mm});
            skLineSegment(sketch, "E96", {"start": v(-26, 2.75) * mm, "end": v(-25.5, 2.75) * mm});
            skLineSegment(sketch, "E97", {"start": v(-25.5, 2.75) * mm, "end": v(-25, 3.25) * mm});
            skLineSegment(sketch, "E98", {"start": v(-25, 3.25) * mm, "end": v(-24.5, 3.25) * mm});
            skLineSegment(sketch, "E99", {"start": v(-24.5, 3.25) * mm, "end": v(-24, 2.75) * mm});
            skLineSegment(sketch, "E100", {"start": v(-24, 2.75) * mm, "end": v(-23.5, 2.75) * mm});
            skLineSegment(sketch, "E101", {"start": v(-23.5, 2.75) * mm, "end": v(-23, 3.25) * mm});
            skLineSegment(sketch, "E102", {"start": v(-23, 3.25) * mm, "end": v(-22.5, 3.25) * mm});
            skLineSegment(sketch, "E103", {"start": v(-22.5, 3.25) * mm, "end": v(-22, 2.75) * mm});
            skSolve(sketch);
        }
        {
            var Q0;
            {var subQ0=sQuery(id+"F11.wireOp",EDGE,"E77");Q0=makeQuery(id+"F11.imprint","IMPRINT",FACE,{"disambiguationData":[TD([[makeQuery(id+"F11.imprint","IMPRINT",EDGE,{"derivedFrom":subQ0}),-1.0]])]});}
            var Q1;
            {var subQ0=sQuery(id+"F11.wireOp",EDGE,"E81");Q1=makeQuery(id+"F11.imprint","IMPRINT",FACE,{"disambiguationData":[TD([[makeQuery(id+"F11.imprint","IMPRINT",EDGE,{"derivedFrom":subQ0}),-1.0]])]});}
            var Q2;
            {var subQ0=sQuery(id+"F11.wireOp",EDGE,"E85");Q2=makeQuery(id+"F11.imprint","IMPRINT",FACE,{"disambiguationData":[TD([[makeQuery(id+"F11.imprint","IMPRINT",EDGE,{"derivedFrom":subQ0}),-1.0]])]});}
            var Q3;
            {var subQ0=sQuery(id+"F11.wireOp",EDGE,"E89");Q3=makeQuery(id+"F11.imprint","IMPRINT",FACE,{"disambiguationData":[TD([[makeQuery(id+"F11.imprint","IMPRINT",EDGE,{"derivedFrom":subQ0}),-1.0]])]});}
            var Q4;
            {var subQ0=sQuery(id+"F11.wireOp",EDGE,"E93");Q4=makeQuery(id+"F11.imprint","IMPRINT",FACE,{"disambiguationData":[TD([[makeQuery(id+"F11.imprint","IMPRINT",EDGE,{"derivedFrom":subQ0}),-1.0]])]});}
            var Q5;
            {var subQ0=sQuery(id+"F11.wireOp",EDGE,"E97");Q5=makeQuery(id+"F11.imprint","IMPRINT",FACE,{"disambiguationData":[TD([[makeQuery(id+"F11.imprint","IMPRINT",EDGE,{"derivedFrom":subQ0}),-1.0]])]});}
            var Q6;
            {var subQ0=sQuery(id+"F11.wireOp",EDGE,"E101");Q6=makeQuery(id+"F11.imprint","IMPRINT",FACE,{"disambiguationData":[TD([[makeQuery(id+"F11.imprint","IMPRINT",EDGE,{"derivedFrom":subQ0}),-1.0]])]});}
            var Q7;
            Q7=makeQuery(id+"F4.boolean.opBoolean","COPY",FACE,{"derivedFrom":makeQuery(id+"F4.opExtrude","SWEPT_FACE",FACE,{"disambiguationData":[OSD([sQuery(id+"F3.wireOp",EDGE,"E31.top")])]})});
            extrude(context, id + "F12", {"entities" : qUnion([Q0, Q1, Q2, Q3, Q4, Q5, Q6]), "operationType" : NewBodyOperationType.ADD, "endBound" : BoundingType.UP_TO_SURFACE, "depth" : 25 * mm, "endBoundEntityFace" : qUnion([Q7]), "offsetDistance" : 25 * mm});
        }
        {
            var Q0;
            Q0=makeQuery(id+"F4.boolean.opBoolean","COPY",FACE,{"derivedFrom":makeQuery(id+"F4.opExtrude","SWEPT_FACE",FACE,{"disambiguationData":[OSD([sQuery(id+"F3.wireOp",EDGE,"E28")])]})});
            var sketch = newSketch(context, id + "F13", { "sketchPlane" : qUnion([Q0])});
            skLineSegment(sketch, "E104", {"start": v(-36, 2.75) * mm, "end": v(-35.5, 2.75) * mm});
            skLineSegment(sketch, "E105", {"start": v(-35.5, 2.75) * mm, "end": v(-35, 3.25) * mm});
            skLineSegment(sketch, "E106", {"start": v(-35, 3.25) * mm, "end": v(-34.5, 3.25) * mm});
            skLineSegment(sketch, "E107", {"start": v(-34.5, 3.25) * mm, "end": v(-34, 2.75) * mm});
            skLineSegment(sketch, "E108", {"start": v(-34, 2.75) * mm, "end": v(-33.5, 2.75) * mm});
            skLineSegment(sketch, "E109", {"start": v(-33.5, 2.75) * mm, "end": v(-33, 3.25) * mm});
            skLineSegment(sketch, "E110", {"start": v(-33, 3.25) * mm, "end": v(-32.5, 3.25) * mm});
            skLineSegment(sketch, "E111", {"start": v(-32.5, 3.25) * mm, "end": v(-32, 2.75) * mm});
            skLineSegment(sketch, "E112", {"start": v(-32, 2.75) * mm, "end": v(-31.5, 2.75) * mm});
            skLineSegment(sketch, "E113", {"start": v(-31.5, 2.75) * mm, "end": v(-31, 3.25) * mm});
            skLineSegment(sketch, "E114", {"start": v(-31, 3.25) * mm, "end": v(-30.5, 3.25) * mm});
            skLineSegment(sketch, "E115", {"start": v(-30.5, 3.25) * mm, "end": v(-30, 2.75) * mm});
            skLineSegment(sketch, "E116", {"start": v(-30, 2.75) * mm, "end": v(-29.5, 2.75) * mm});
            skLineSegment(sketch, "E117", {"start": v(-29.5, 2.75) * mm, "end": v(-29, 3.25) * mm});
            skLineSegment(sketch, "E118", {"start": v(-29, 3.25) * mm, "end": v(-28.5, 3.25) * mm});
            skLineSegment(sketch, "E119", {"start": v(-28.5, 3.25) * mm, "end": v(-28, 2.75) * mm});
            skLineSegment(sketch, "E120", {"start": v(-28, 2.75) * mm, "end": v(-27.5, 2.75) * mm});
            skLineSegment(sketch, "E121", {"start": v(-27.5, 2.75) * mm, "end": v(-27, 3.25) * mm});
            skLineSegment(sketch, "E122", {"start": v(-27, 3.25) * mm, "end": v(-26.5, 3.25) * mm});
            skLineSegment(sketch, "E123", {"start": v(-26.5, 3.25) * mm, "end": v(-26, 2.75) * mm});
            skLineSegment(sketch, "E124", {"start": v(-26, 2.75) * mm, "end": v(-25.5, 2.75) * mm});
            skLineSegment(sketch, "E125", {"start": v(-25.5, 2.75) * mm, "end": v(-25, 3.25) * mm});
            skLineSegment(sketch, "E126", {"start": v(-25, 3.25) * mm, "end": v(-24.5, 3.25) * mm});
            skLineSegment(sketch, "E127", {"start": v(-24.5, 3.25) * mm, "end": v(-24, 2.75) * mm});
            skLineSegment(sketch, "E128", {"start": v(-24, 2.75) * mm, "end": v(-23.5, 2.75) * mm});
            skLineSegment(sketch, "E129", {"start": v(-23.5, 2.75) * mm, "end": v(-23, 3.25) * mm});
            skLineSegment(sketch, "E130", {"start": v(-23, 3.25) * mm, "end": v(-22.5, 3.25) * mm});
            skLineSegment(sketch, "E131", {"start": v(-22.5, 3.25) * mm, "end": v(-22, 2.75) * mm});
            skSolve(sketch);
        }
        {
            var Q0;
            {var subQ0=sQuery(id+"F13.wireOp",EDGE,"E125");Q0=makeQuery(id+"F13.imprint","IMPRINT",FACE,{"disambiguationData":[TD([[makeQuery(id+"F13.imprint","IMPRINT",EDGE,{"derivedFrom":subQ0}),-1.0]])]});}
            var Q1;
            {var subQ0=sQuery(id+"F13.wireOp",EDGE,"E121");Q1=makeQuery(id+"F13.imprint","IMPRINT",FACE,{"disambiguationData":[TD([[makeQuery(id+"F13.imprint","IMPRINT",EDGE,{"derivedFrom":subQ0}),-1.0]])]});}
            var Q2;
            {var subQ0=sQuery(id+"F13.wireOp",EDGE,"E129");Q2=makeQuery(id+"F13.imprint","IMPRINT",FACE,{"disambiguationData":[TD([[makeQuery(id+"F13.imprint","IMPRINT",EDGE,{"derivedFrom":subQ0}),-1.0]])]});}
            var Q3;
            {var subQ0=sQuery(id+"F13.wireOp",EDGE,"E117");Q3=makeQuery(id+"F13.imprint","IMPRINT",FACE,{"disambiguationData":[TD([[makeQuery(id+"F13.imprint","IMPRINT",EDGE,{"derivedFrom":subQ0}),-1.0]])]});}
            var Q4;
            {var subQ0=sQuery(id+"F13.wireOp",EDGE,"E113");Q4=makeQuery(id+"F13.imprint","IMPRINT",FACE,{"disambiguationData":[TD([[makeQuery(id+"F13.imprint","IMPRINT",EDGE,{"derivedFrom":subQ0}),-1.0]])]});}
            var Q5;
            {var subQ0=sQuery(id+"F13.wireOp",EDGE,"E109");Q5=makeQuery(id+"F13.imprint","IMPRINT",FACE,{"disambiguationData":[TD([[makeQuery(id+"F13.imprint","IMPRINT",EDGE,{"derivedFrom":subQ0}),-1.0]])]});}
            var Q6;
            {var subQ0=sQuery(id+"F13.wireOp",EDGE,"E105");Q6=makeQuery(id+"F13.imprint","IMPRINT",FACE,{"disambiguationData":[TD([[makeQuery(id+"F13.imprint","IMPRINT",EDGE,{"derivedFrom":subQ0}),-1.0]])]});}
            var Q7;
            Q7=makeQuery(id+"F4.boolean.opBoolean","COPY",FACE,{"derivedFrom":makeQuery(id+"F4.opExtrude","SWEPT_FACE",FACE,{"disambiguationData":[OSD([sQuery(id+"F3.wireOp",EDGE,"E26")])]})});
            extrude(context, id + "F14", {"entities" : qUnion([Q0, Q1, Q2, Q3, Q4, Q5, Q6]), "operationType" : NewBodyOperationType.ADD, "endBound" : BoundingType.UP_TO_SURFACE, "depth" : 25 * mm, "endBoundEntityFace" : qUnion([Q7]), "offsetDistance" : 25 * mm});
        }
        {
            var Q0;
            Q0=makeQuery(id+"F3.imprint","IMPRINT",FACE,{"disambiguationData":[TD([[makeQuery(id+"F3.imprint","IMPRINT",EDGE,{"derivedFrom":sQuery(id+"F3.wireOp",EDGE,"E49.bottom")}),-1.0]])]});
            extrude(context, id + "F15", {"entities" : qUnion([Q0]), "operationType" : NewBodyOperationType.REMOVE, "endBound" : BoundingType.THROUGH_ALL, "oppositeDirection" : true, "depth" : 25 * mm, "offsetDistance" : 25 * mm});
        }
        {
            var Q0;
            Q0=makeQuery(id+"F15.boolean.opBoolean","INTERSECT",EDGE,{"derivedFrom":[makeQuery(id+"F1.opExtrude","CAP_FACE",FACE,{"disambiguationData":[OSD([sQuery(id+"F0.wireOp",EDGE,"E2"),sQuery(id+"F0.wireOp",EDGE,"E3"),sQuery(id+"F0.wireOp",EDGE,"E4"),sQuery(id+"F0.wireOp",EDGE,"E5"),sQuery(id+"F0.wireOp",EDGE,"E8"),sQuery(id+"F0.wireOp",EDGE,"E14"),sQuery(id+"F0.wireOp",EDGE,"E15"),sQuery(id+"F0.wireOp",EDGE,"E17"),sQuery(id+"F0.wireOp",EDGE,"E18"),sQuery(id+"F0.wireOp",EDGE,"E19"),sQuery(id+"F0.wireOp",EDGE,"E20"),sQuery(id+"F0.wireOp",EDGE,"E21"),sQuery(id+"F0.wireOp",EDGE,"E22"),sQuery(id+"F0.wireOp",EDGE,"E23")])],"isStart":true}),makeQuery(id+"F15.opExtrude","SWEPT_FACE",FACE,{"disambiguationData":[OSD([sQuery(id+"F3.wireOp",EDGE,"E49.top")])]})]});
            chamfer(context, id + "F16", {"entities" : qUnion([Q0]), "chamferType" : ChamferType.OFFSET_ANGLE, "width" : 3 * mm, "oppositeDirection" : false, "angle" : 45 * degree, "tangentPropagation" : true});
        }
        {
            var Q0;
            Q0=makeQuery(id+"F1.opExtrude","CAP_EDGE",EDGE,{"disambiguationData":[OSD([sQuery(id+"F0.wireOp",EDGE,"E2")])],"isStart":true});
            chamfer(context, id + "F17", {"entities" : qUnion([Q0]), "chamferType" : ChamferType.OFFSET_ANGLE, "width" : 1.4 * mm, "oppositeDirection" : false, "angle" : 35 * degree, "tangentPropagation" : true});
        }
    });
